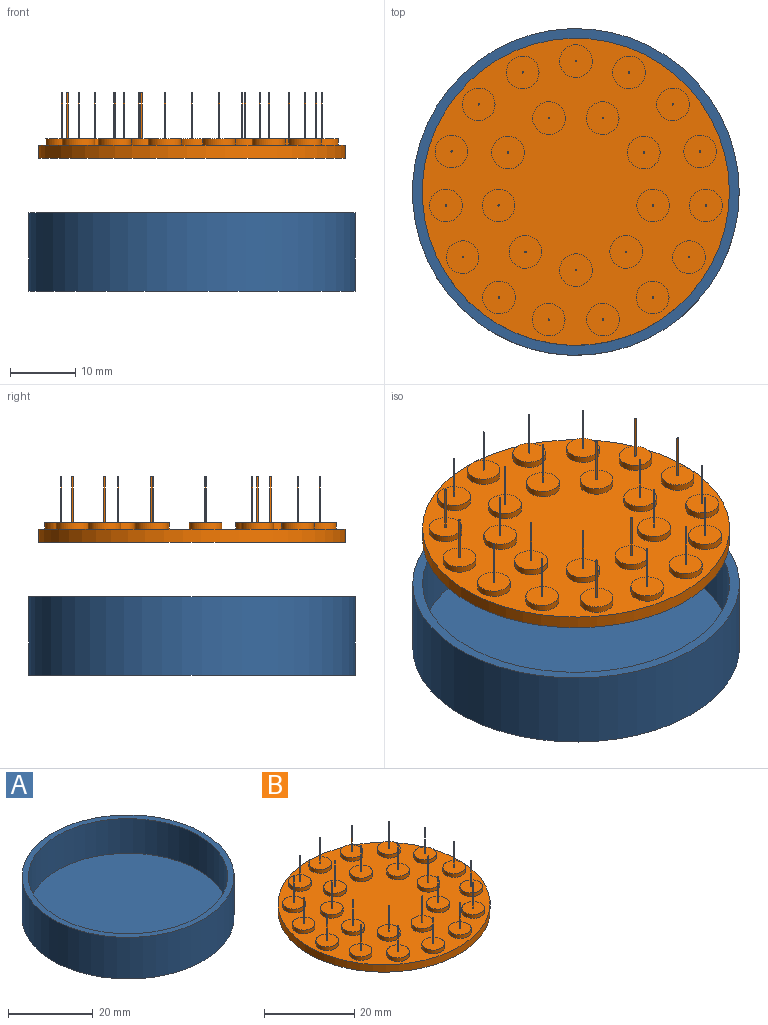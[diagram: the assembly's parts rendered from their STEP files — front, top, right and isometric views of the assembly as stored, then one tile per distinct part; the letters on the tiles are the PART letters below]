
ASSEMBLY  parts=2 mates=1
PART A: 5 faces, bbox 50x50x12 mm
  f0: cylinder r=25mm len=50mm, axis (0,0,1), area 1885mm2, adj f1,f3
  f1: plane 50x50mm, normal (0,0,-1), area 1963.5mm2, adj f0
  f2: cylinder r=23.5mm len=47mm, axis (0,0,-1), area 1476.5mm2, adj f3,f4
  f3: plane 50x50mm, normal (0,0,1), area 228.6mm2, adj f0,f2
  f4: plane 47x47mm, normal (0,0,1), area 1734.9mm2, adj f2
PART B: 99 faces, bbox 47x47x10 mm
  f0: cylinder r=23.5mm len=47mm, axis (0,0,1), area 295.3mm2, adj f1,f2
  f1: plane 47x47mm, normal (0,0,-1), area 1734.9mm2, adj f0
  f2: plane 47x47mm, normal (0,0,1), area 1263.7mm2, adj f0,f3,f7,f11,f15,f19,f23,f27
  f3: cylinder r=2.5mm len=5mm, axis (0,0,-1), area 15.7mm2, adj f2,f4
  f4: plane 5x5mm, normal (0,0,1), area 19.6mm2, adj f3,f6
  f5: plane 0.2x0.2mm, normal (0,0,1), area 0mm2, adj f6
  f6: cylinder r=0.1mm len=7mm, axis (0,0,-1), area 4.4mm2, adj f4,f5
  f7: cylinder r=2.5mm len=5mm, axis (0,0,-1), area 15.7mm2, adj f2,f8
  f8: plane 5x5mm, normal (0,0,1), area 19.6mm2, adj f7,f10
  f9: plane 0.2x0.2mm, normal (0,0,1), area 0mm2, adj f10
  f10: cylinder r=0.1mm len=7mm, axis (0,0,-1), area 4.4mm2, adj f8,f9
  f11: cylinder r=2.5mm len=5mm, axis (0,0,-1), area 15.7mm2, adj f2,f12
  f12: plane 5x5mm, normal (0,0,1), area 19.6mm2, adj f11,f14
  f13: plane 0.2x0.2mm, normal (0,0,1), area 0mm2, adj f14
  f14: cylinder r=0.1mm len=7mm, axis (0,0,-1), area 4.4mm2, adj f12,f13
  f15: cylinder r=2.5mm len=5mm, axis (0,0,-1), area 15.7mm2, adj f2,f16
  f16: plane 5x5mm, normal (0,0,1), area 19.6mm2, adj f15,f18
  f17: plane 0.2x0.2mm, normal (0,0,1), area 0mm2, adj f18
  f18: cylinder r=0.1mm len=7mm, axis (0,0,-1), area 4.4mm2, adj f16,f17
  f19: cylinder r=2.5mm len=5mm, axis (0,0,-1), area 15.7mm2, adj f2,f20
  f20: plane 5x5mm, normal (0,0,1), area 19.6mm2, adj f19,f22
  f21: plane 0.2x0.2mm, normal (0,0,1), area 0mm2, adj f22
  f22: cylinder r=0.1mm len=7mm, axis (0,0,-1), area 4.4mm2, adj f20,f21
  f23: cylinder r=2.5mm len=5mm, axis (0,0,-1), area 15.7mm2, adj f2,f24
  f24: plane 5x5mm, normal (0,0,1), area 19.6mm2, adj f23,f26
  f25: plane 0.2x0.2mm, normal (0,0,1), area 0mm2, adj f26
  f26: cylinder r=0.1mm len=7mm, axis (0,0,-1), area 4.4mm2, adj f24,f25
  f27: cylinder r=2.5mm len=5mm, axis (0,0,-1), area 15.7mm2, adj f2,f28
  f28: plane 5x5mm, normal (0,0,1), area 19.6mm2, adj f27,f30
  f29: plane 0.2x0.2mm, normal (0,0,1), area 0mm2, adj f30
  f30: cylinder r=0.1mm len=7mm, axis (0,0,-1), area 4.4mm2, adj f28,f29
  f31: cylinder r=2.5mm len=5mm, axis (0,0,-1), area 15.7mm2, adj f2,f32
  f32: plane 5x5mm, normal (0,0,1), area 19.6mm2, adj f31,f34
  f33: plane 0.2x0.2mm, normal (0,0,1), area 0mm2, adj f34
  f34: cylinder r=0.1mm len=7mm, axis (0,0,-1), area 4.4mm2, adj f32,f33
  f35: cylinder r=2.5mm len=5mm, axis (0,0,-1), area 15.7mm2, adj f2,f36
  f36: plane 5x5mm, normal (0,0,1), area 19.6mm2, adj f35,f38
  f37: plane 0.2x0.2mm, normal (0,0,1), area 0mm2, adj f38
  f38: cylinder r=0.1mm len=7mm, axis (0,0,-1), area 4.4mm2, adj f36,f37
  f39: cylinder r=2.5mm len=5mm, axis (0,0,-1), area 15.7mm2, adj f2,f40
  f40: plane 5x5mm, normal (0,0,1), area 19.6mm2, adj f39,f42
  f41: plane 0.2x0.2mm, normal (0,0,1), area 0mm2, adj f42
  f42: cylinder r=0.1mm len=7mm, axis (0,0,-1), area 4.4mm2, adj f40,f41
  f43: cylinder r=2.5mm len=5mm, axis (0,0,-1), area 15.7mm2, adj f2,f44
  f44: plane 5x5mm, normal (0,0,1), area 19.6mm2, adj f43,f46
  f45: plane 0.2x0.2mm, normal (0,0,1), area 0mm2, adj f46
  f46: cylinder r=0.1mm len=7mm, axis (0,0,-1), area 4.4mm2, adj f44,f45
  f47: cylinder r=2.5mm len=5mm, axis (0,0,-1), area 15.7mm2, adj f2,f48
  f48: plane 5x5mm, normal (0,0,1), area 19.6mm2, adj f47,f50
  f49: plane 0.2x0.2mm, normal (0,0,1), area 0mm2, adj f50
  f50: cylinder r=0.1mm len=7mm, axis (0,0,-1), area 4.4mm2, adj f48,f49
  f51: cylinder r=2.5mm len=5mm, axis (0,0,-1), area 15.7mm2, adj f2,f52
  f52: plane 5x5mm, normal (0,0,1), area 19.6mm2, adj f51,f54
  f53: plane 0.2x0.2mm, normal (0,0,1), area 0mm2, adj f54
  f54: cylinder r=0.1mm len=7mm, axis (0,0,-1), area 4.4mm2, adj f52,f53
  f55: cylinder r=2.5mm len=5mm, axis (0,0,-1), area 15.7mm2, adj f2,f56
  f56: plane 5x5mm, normal (0,0,1), area 19.6mm2, adj f55,f58
  f57: plane 0.2x0.2mm, normal (0,0,1), area 0mm2, adj f58
  f58: cylinder r=0.1mm len=7mm, axis (0,0,-1), area 4.4mm2, adj f56,f57
  f59: cylinder r=2.5mm len=5mm, axis (0,0,-1), area 15.7mm2, adj f2,f60
  f60: plane 5x5mm, normal (0,0,1), area 19.6mm2, adj f59,f62
  f61: plane 0.2x0.2mm, normal (0,0,1), area 0mm2, adj f62
  f62: cylinder r=0.1mm len=7mm, axis (0,0,-1), area 4.4mm2, adj f60,f61
  f63: cylinder r=2.5mm len=5mm, axis (0,0,-1), area 15.7mm2, adj f2,f64
  f64: plane 5x5mm, normal (0,0,1), area 19.6mm2, adj f63,f66
  f65: plane 0.2x0.2mm, normal (0,0,1), area 0mm2, adj f66
  f66: cylinder r=0.1mm len=7mm, axis (0,0,-1), area 4.4mm2, adj f64,f65
  f67: cylinder r=2.5mm len=5mm, axis (0,0,-1), area 15.7mm2, adj f2,f68
  f68: plane 5x5mm, normal (0,0,1), area 19.6mm2, adj f67,f70
  f69: plane 0.2x0.2mm, normal (0,0,1), area 0mm2, adj f70
  f70: cylinder r=0.1mm len=7mm, axis (0,0,-1), area 4.4mm2, adj f68,f69
  f71: cylinder r=2.5mm len=5mm, axis (0,0,-1), area 15.7mm2, adj f2,f72
  f72: plane 5x5mm, normal (0,0,1), area 19.6mm2, adj f71,f74
  f73: plane 0.2x0.2mm, normal (0,0,1), area 0mm2, adj f74
  f74: cylinder r=0.1mm len=7mm, axis (0,0,-1), area 4.4mm2, adj f72,f73
  f75: cylinder r=2.5mm len=5mm, axis (0,0,-1), area 15.7mm2, adj f2,f76
  f76: plane 5x5mm, normal (0,0,1), area 19.6mm2, adj f75,f78
  f77: plane 0.2x0.2mm, normal (0,0,1), area 0mm2, adj f78
  f78: cylinder r=0.1mm len=7mm, axis (0,0,-1), area 4.4mm2, adj f76,f77
  f79: cylinder r=2.5mm len=5mm, axis (0,0,-1), area 15.7mm2, adj f2,f80
  f80: plane 5x5mm, normal (0,0,1), area 19.6mm2, adj f79,f82
  f81: plane 0.2x0.2mm, normal (0,0,1), area 0mm2, adj f82
  f82: cylinder r=0.1mm len=7mm, axis (0,0,-1), area 4.4mm2, adj f80,f81
  f83: cylinder r=2.5mm len=5mm, axis (0,0,-1), area 15.7mm2, adj f2,f84
  f84: plane 5x5mm, normal (0,0,1), area 19.6mm2, adj f83,f86
  f85: plane 0.2x0.2mm, normal (0,0,1), area 0mm2, adj f86
  f86: cylinder r=0.1mm len=7mm, axis (0,0,-1), area 4.4mm2, adj f84,f85
  f87: cylinder r=2.5mm len=5mm, axis (0,0,-1), area 15.7mm2, adj f2,f88
  f88: plane 5x5mm, normal (0,0,1), area 19.6mm2, adj f87,f90
  f89: plane 0.2x0.2mm, normal (0,0,1), area 0mm2, adj f90
  f90: cylinder r=0.1mm len=7mm, axis (0,0,-1), area 4.4mm2, adj f88,f89
  f91: cylinder r=2.5mm len=5mm, axis (0,0,-1), area 15.7mm2, adj f2,f92
  f92: plane 5x5mm, normal (0,0,1), area 19.6mm2, adj f91,f94
  f93: plane 0.2x0.2mm, normal (0,0,1), area 0mm2, adj f94
  f94: cylinder r=0.1mm len=7mm, axis (0,0,-1), area 4.4mm2, adj f92,f93
  f95: cylinder r=2.5mm len=5mm, axis (0,0,-1), area 15.7mm2, adj f2,f96
  f96: plane 5x5mm, normal (0,0,1), area 19.6mm2, adj f95,f98
  f97: plane 0.2x0.2mm, normal (0,0,1), area 0mm2, adj f98
  f98: cylinder r=0.1mm len=7mm, axis (0,0,-1), area 4.4mm2, adj f96,f97
PLACE A at identity fixed
PLACE B t=(0,0,10.35)mm
MATE slider A.f2 <-> B.f0  axis (0,0,1) through (0,0,10)mm
